# Revit family: Gorter-B_0800-0800
name_source: partatom
category: Generic Models
revit_build: Autodesk Revit 2017 (Build: 20171027_0315(x64)
units: mm (PartAtom-declared; Revit-internal decimal feet)

## family parameters
Always vertical = Yes
Can host rebar = No
Cut with Voids When Loaded = No
Host = Wall
Part Type = Normal
Room Calculation Point = No
Round Connector Dimension = Use Diameter
Shared = Yes

## types (4) — shared parameters
Bevestiging = voorgeboorde bevestigingsgaten
E = 120 minuten
EW = 120 minuten
El-1 = 20 minuten
El-2 = 60 minuten
Model = Wandluik B, 120 minuten brandwerend
URL = https://www.gortergroup.com
afstand tot wand = 2 mm  [stored 0.00656168 ft]
brandwerende vulling = isolatievulling
draairichting aanzicht = Yes
draairichting plattegrond = Yes
frame = KTL behandeld staal - RAL9010
wandluik = KTL behandeld staal - RAL9010

## per-type parameters (varying)
| type | A | B | Sparingsmaat A | Sparingsmaat B | Weight (kg) |
| B-0400-0400 | 400 mm  [stored 1.31234 ft] | 400 mm  [stored 1.31234 ft] | 453 mm  [stored 1.48622 ft] | 453 mm  [stored 1.48622 ft] | 14 |
| B-0600-0600 | 600 mm | 600 mm | 653 mm  [stored 2.14239 ft] | 653 mm  [stored 2.14239 ft] | 27 |
| B-0600-0800 | 600 mm | 800 mm  [stored 2.62467 ft] | 653 mm  [stored 2.14239 ft] | 853 mm  [stored 2.79856 ft] | 34 |
| B-0800-0800 | 800 mm  [stored 2.62467 ft] | 800 mm  [stored 2.62467 ft] | 853 mm  [stored 2.79856 ft] | 853 mm  [stored 2.79856 ft] | 43 |

note: [stored X ft] marks values corroborated as IEEE doubles in the binary element streams (Revit-internal decimal feet)

## geometry (parser evidence)
native form markers: Sweep x3
no freeform markers — native parametric forms only
